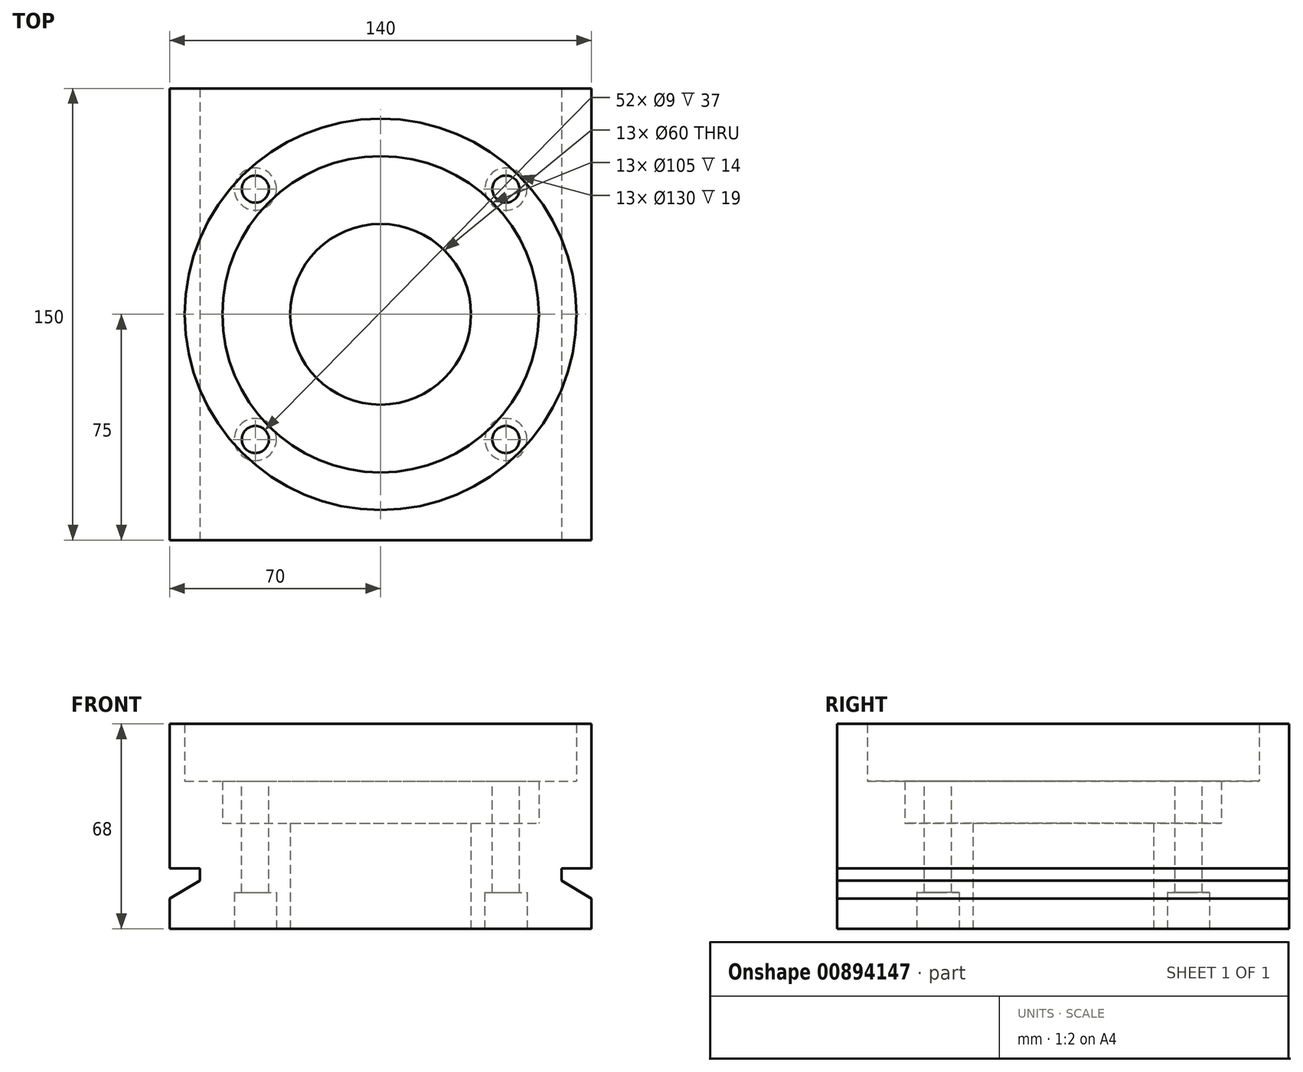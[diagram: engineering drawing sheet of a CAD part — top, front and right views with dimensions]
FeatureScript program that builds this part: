
annotation { "Feature Type Name" : "Feature", "Feature Type Description" : "" }
export const myFeature = defineFeature(function(context is Context, id is Id, definition is map)
    precondition{}
    {
        {
            var Q0;
            Q0=qCreatedBy(makeId("Front.planeOp"),FACE);
            var sketch = newSketch(context, id + "F0", { "sketchPlane" : qUnion([Q0])});
            skLineSegment(sketch, "E0", {"start": v(0, 0) * mm, "end": v(70, 0) * mm});
            skLineSegment(sketch, "E1", {"start": v(70, 0) * mm, "end": v(70, 68) * mm});
            skLineSegment(sketch, "E2", {"start": v(70, 68) * mm, "end": v(-70, 68) * mm});
            skLineSegment(sketch, "E3", {"start": v(-70, 68) * mm, "end": v(-70, 0) * mm});
            skLineSegment(sketch, "E4", {"start": v(-70, 0) * mm, "end": v(0, 0) * mm});
            skSolve(sketch);
        }
        {
            var Q0;
            Q0=makeQuery(id+"F0.imprint","IMPRINT",FACE,{"disambiguationData":[TD([[makeQuery(id+"F0.imprint","IMPRINT",EDGE,{"derivedFrom":sQuery(id+"F0.wireOp",EDGE,"E0")}),1.0]])]});
            extrude(context, id + "F1", {"entities" : qUnion([Q0]), "endBound" : BoundingType.SYMMETRIC, "depth" : 150 * mm, "offsetDistance" : 25 * mm});
        }
        {
            var Q0;
            Q0=qCreatedBy(makeId("Front.planeOp"),FACE);
            var sketch = newSketch(context, id + "F2", { "sketchPlane" : qUnion([Q0])});
            skLineSegment(sketch, "E5", {"start": v(0, 0) * mm, "end": v(30, 0) * mm});
            skLineSegment(sketch, "E6", {"start": v(30, 0) * mm, "end": v(30, 35) * mm});
            skLineSegment(sketch, "E7", {"start": v(30, 35) * mm, "end": v(52.5, 35) * mm});
            skLineSegment(sketch, "E8", {"start": v(52.5, 35) * mm, "end": v(52.5, 49) * mm});
            skLineSegment(sketch, "E9", {"start": v(52.5, 49) * mm, "end": v(65, 49) * mm});
            skLineSegment(sketch, "E10", {"start": v(65, 49) * mm, "end": v(65, 68) * mm});
            skLineSegment(sketch, "E11", {"start": v(0, 0) * mm, "end": v(0, 68) * mm});
            skLineSegment(sketch, "E12", {"start": v(0, 68) * mm, "end": v(65, 68) * mm});
            skSolve(sketch);
        }
        {
            var Q0;
            Q0 = qSketchRegion(id + "F2", true);
            var Q1;
            Q1=sQuery(id+"F2.wireOp",EDGE,"E11");
            revolve(context, id + "F3", {"operationType" : NewBodyOperationType.REMOVE, "surfaceOperationType" : NewSurfaceOperationType.NEW, "entities" : qUnion([Q0]), "axis" : qUnion([Q1]), "revolveType" : RevolveType.FULL});
        }
        {
            var Q0;
            Q0=makeQuery(id+"F3.boolean.opBoolean","COPY",FACE,{"derivedFrom":makeQuery(id+"F3.opRevolve","SWEPT_FACE",FACE,{"disambiguationData":[OSD([sQuery(id+"F2.wireOp",EDGE,"E7")])]})});
            var sketch = newSketch(context, id + "F4", { "sketchPlane" : qUnion([Q0])});
            skCircle(sketch, "E13", {"center": v(41.58, 41.58) * mm, "radius": 4.5 * mm});
            skCircle(sketch, "E14", {"center": v(41.58, -41.58) * mm, "radius": 4.5 * mm});
            skCircle(sketch, "E15", {"center": v(-41.58, -41.58) * mm, "radius": 4.5 * mm});
            skCircle(sketch, "E16", {"center": v(-41.58, 41.58) * mm, "radius": 4.5 * mm});
            skSolve(sketch);
        }
        {
            var Q0;
            Q0=makeQuery(id+"F1.opExtrude","SWEPT_FACE",FACE,{"disambiguationData":[OSD([sQuery(id+"F0.wireOp",EDGE,"E0"),sQuery(id+"F0.wireOp",EDGE,"E4")])]});
            var sketch = newSketch(context, id + "F5", { "sketchPlane" : qUnion([Q0])});
            skCircle(sketch, "E17", {"center": v(-41.58, 41.58) * mm, "radius": 7 * mm});
            skCircle(sketch, "E18", {"center": v(41.58, 41.58) * mm, "radius": 7 * mm});
            skCircle(sketch, "E19", {"center": v(41.58, -41.58) * mm, "radius": 7 * mm});
            skCircle(sketch, "E20", {"center": v(-41.58, -41.58) * mm, "radius": 7 * mm});
            skSolve(sketch);
        }
        {
            var Q0;
            Q0=makeQuery(id+"F5.imprint","IMPRINT",FACE,{"disambiguationData":[TD([[makeQuery(id+"F5.imprint","IMPRINT",EDGE,{"derivedFrom":sQuery(id+"F5.wireOp",EDGE,"E18")}),1.0]])]});
            var Q1;
            Q1=makeQuery(id+"F5.imprint","IMPRINT",FACE,{"disambiguationData":[TD([[makeQuery(id+"F5.imprint","IMPRINT",EDGE,{"derivedFrom":sQuery(id+"F5.wireOp",EDGE,"E19")}),1.0]])]});
            var Q2;
            Q2=makeQuery(id+"F5.imprint","IMPRINT",FACE,{"disambiguationData":[TD([[makeQuery(id+"F5.imprint","IMPRINT",EDGE,{"derivedFrom":sQuery(id+"F5.wireOp",EDGE,"E20")}),1.0]])]});
            var Q3;
            Q3=makeQuery(id+"F5.imprint","IMPRINT",FACE,{"disambiguationData":[TD([[makeQuery(id+"F5.imprint","IMPRINT",EDGE,{"derivedFrom":sQuery(id+"F5.wireOp",EDGE,"E17")}),1.0]])]});
            extrude(context, id + "F6", {"entities" : qUnion([Q0, Q1, Q2, Q3]), "operationType" : NewBodyOperationType.REMOVE, "oppositeDirection" : true, "depth" : 12 * mm, "offsetDistance" : 25 * mm});
        }
        {
            var Q0;
            Q0 = qSketchRegion(id + "F4", true);
            extrude(context, id + "F7", {"entities" : qUnion([Q0]), "operationType" : NewBodyOperationType.REMOVE, "endBound" : BoundingType.SYMMETRIC, "oppositeDirection" : true, "depth" : 74 * mm, "offsetDistance" : 25 * mm});
        }
        {
            var Q0;
            Q0=makeQuery(id+"F1.opExtrude","CAP_FACE",FACE,{"disambiguationData":[OSD([sQuery(id+"F0.wireOp",EDGE,"E0"),sQuery(id+"F0.wireOp",EDGE,"E1"),sQuery(id+"F0.wireOp",EDGE,"E2"),sQuery(id+"F0.wireOp",EDGE,"E3"),sQuery(id+"F0.wireOp",EDGE,"E4")])],"isStart":false});
            var sketch = newSketch(context, id + "F8", { "sketchPlane" : qUnion([Q0])});
            skLineSegment(sketch, "E21", {"start": v(70, 10) * mm, "end": v(70, 20) * mm});
            skLineSegment(sketch, "E22", {"start": v(70, 20) * mm, "end": v(60, 20) * mm});
            skLineSegment(sketch, "E23", {"start": v(60, 20) * mm, "end": v(60, 16) * mm});
            skLineSegment(sketch, "E24", {"start": v(60, 16) * mm, "end": v(70, 10) * mm});
            skLineSegment(sketch, "E25.MirrorCS", {"start": v(-60, 20) * mm, "end": v(-60, 16) * mm});
            skLineSegment(sketch, "E26.MirrorCS", {"start": v(-60, 16) * mm, "end": v(-70, 10) * mm});
            skLineSegment(sketch, "E27.MirrorCS", {"start": v(-70, 10) * mm, "end": v(-70, 20) * mm});
            skLineSegment(sketch, "E28.MirrorCS", {"start": v(-70, 20) * mm, "end": v(-60, 20) * mm});
            skSolve(sketch);
        }
        {
            var Q0;
            Q0 = qSketchRegion(id + "F8", true);
            extrude(context, id + "F9", {"entities" : qUnion([Q0]), "operationType" : NewBodyOperationType.REMOVE, "oppositeDirection" : true, "depth" : 150 * mm, "offsetDistance" : 25 * mm});
        }
    });
